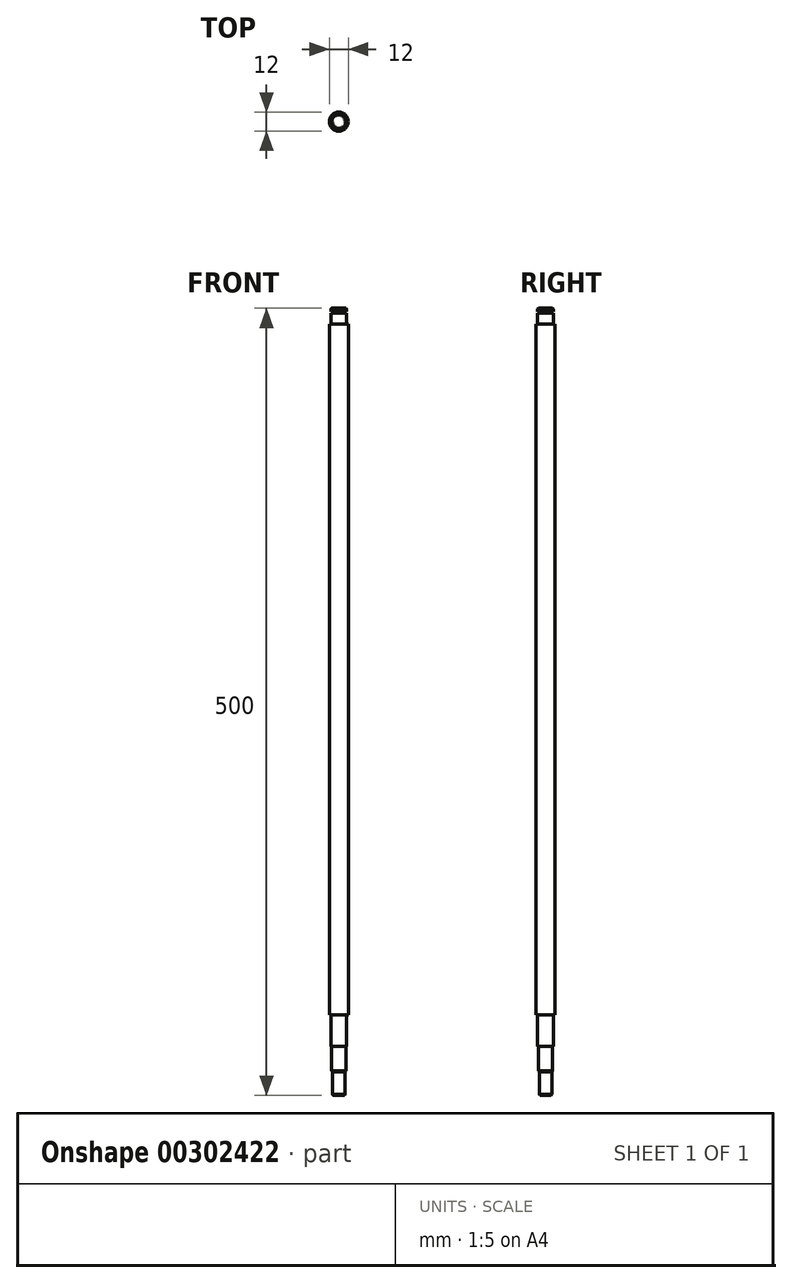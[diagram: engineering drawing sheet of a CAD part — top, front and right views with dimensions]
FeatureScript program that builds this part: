
annotation { "Feature Type Name" : "Feature", "Feature Type Description" : "" }
export const myFeature = defineFeature(function(context is Context, id is Id, definition is map)
    precondition{}
    {
        {
            var Q0;
            Q0=qCreatedBy(makeId("Front.planeOp"),FACE);
            var sketch = newSketch(context, id + "F0", { "sketchPlane" : qUnion([Q0])});
            skLineSegment(sketch, "E0", {"start": v(0, 0) * mm, "end": v(0, 285.84) * mm, "construction": true});
            skLineSegment(sketch, "E1", {"start": v(0, 0) * mm, "end": v(3.5, 0) * mm});
            skLineSegment(sketch, "E2", {"start": v(3.5, 0) * mm, "end": v(4, 0.5) * mm});
            skLineSegment(sketch, "E3", {"start": v(4, 0.5) * mm, "end": v(4, 15) * mm});
            skLineSegment(sketch, "E4", {"start": v(4, 15) * mm, "end": v(4.5, 15.5) * mm});
            skLineSegment(sketch, "E5", {"start": v(4.5, 15.5) * mm, "end": v(4.5, 31) * mm});
            skLineSegment(sketch, "E6", {"start": v(4.5, 31) * mm, "end": v(5, 31) * mm});
            skLineSegment(sketch, "E7", {"start": v(5, 31) * mm, "end": v(5, 51) * mm});
            skLineSegment(sketch, "E8", {"start": v(5, 51) * mm, "end": v(6, 51) * mm});
            skLineSegment(sketch, "E9", {"start": v(6, 51) * mm, "end": v(6, 490) * mm});
            skLineSegment(sketch, "E10", {"start": v(6, 490) * mm, "end": v(5, 490) * mm});
            skLineSegment(sketch, "E11", {"start": v(5, 490) * mm, "end": v(5, 497) * mm});
            skLineSegment(sketch, "E12", {"start": v(5, 497) * mm, "end": v(3.8, 497) * mm});
            skLineSegment(sketch, "E13", {"start": v(3.8, 497) * mm, "end": v(3.8, 497.9) * mm});
            skLineSegment(sketch, "E14", {"start": v(3.8, 497.9) * mm, "end": v(5, 497.9) * mm});
            skLineSegment(sketch, "E15", {"start": v(5, 497.9) * mm, "end": v(5, 499.5) * mm});
            skLineSegment(sketch, "E16", {"start": v(5, 499.5) * mm, "end": v(4.5, 500) * mm});
            skLineSegment(sketch, "E17", {"start": v(4.5, 500) * mm, "end": v(0, 500) * mm});
            skLineSegment(sketch, "E18", {"start": v(0, 500) * mm, "end": v(0, 0) * mm});
            skSolve(sketch);
        }
        {
            var Q0;
            Q0=qSketchRegion(id+"F0",true);
            var Q1;
            Q1=sQuery(id+"F0.wireOp",EDGE,"E0");
            revolve(context, id + "F1", {"entities" : qUnion([Q0]), "axis" : qUnion([Q1]), "revolveType" : RevolveType.FULL});
        }
    });
